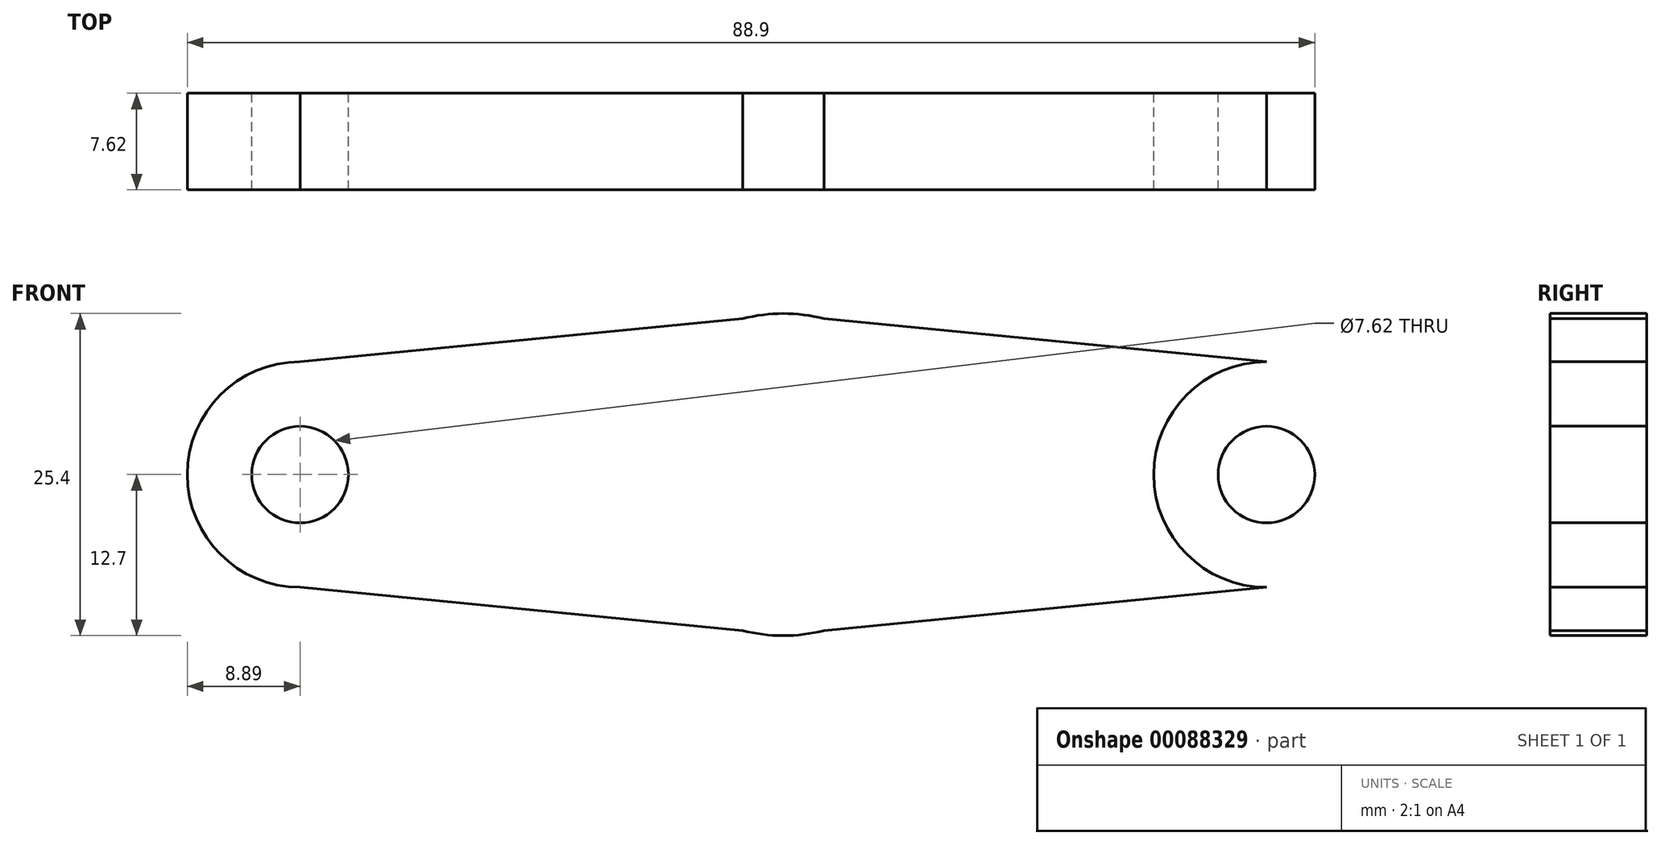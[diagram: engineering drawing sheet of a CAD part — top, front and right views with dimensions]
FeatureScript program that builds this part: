
annotation { "Feature Type Name" : "Feature", "Feature Type Description" : "" }
export const myFeature = defineFeature(function(context is Context, id is Id, definition is map)
    precondition{}
    {
        {
            var Q0;
            Q0=qCreatedBy(makeId("Front.planeOp"),FACE);
            var sketch = newSketch(context, id + "F0", { "sketchPlane" : qUnion([Q0])});
            skCircle(sketch, "E0", {"center": v(0, 0) * mm, "radius": 12.7 * mm});
            skLineSegment(sketch, "E1", {"start": v(0, 0) * mm, "end": v(-38.1, 0) * mm});
            skCircle(sketch, "E2", {"center": v(-38.1, 0) * mm, "radius": 3.81 * mm});
            skCircle(sketch, "E3", {"center": v(-38.1, 0) * mm, "radius": 8.9 * mm});
            skLineSegment(sketch, "E4", {"start": v(-38.1, 0) * mm, "end": v(-38.1, 8.89) * mm});
            skLineSegment(sketch, "E5", {"start": v(-38.1, 8.89) * mm, "end": v(-3.2, 12.3) * mm});
            skLineSegment(sketch, "E6.MirrorCS", {"start": v(-38.1, -8.9) * mm, "end": v(-3.2, -12.3) * mm});
            skCircle(sketch, "E7.MirrorC", {"center": v(38.1, 0) * mm, "radius": 8.9 * mm});
            skLineSegment(sketch, "E8.MirrorCS", {"start": v(38.1, 8.9) * mm, "end": v(3.2, 12.3) * mm});
            skLineSegment(sketch, "E9.MirrorCS", {"start": v(38.1, -8.89) * mm, "end": v(3.2, -12.3) * mm});
            skCircle(sketch, "E10.MirrorC", {"center": v(38.1, 0) * mm, "radius": 3.81 * mm});
            skLineSegment(sketch, "E11.MirrorCS", {"start": v(38.1, 0) * mm, "end": v(38.1, 8.9) * mm});
            skSolve(sketch);
        }
        {
            var Q0;
            {var subQ0=sQuery(id+"F0.wireOp",EDGE,"E5");Q0=makeQuery(id+"F0.imprint","IMPRINT",FACE,{"disambiguationData":[TD([[makeQuery(id+"F0.imprint","IMPRINT",EDGE,{"derivedFrom":subQ0}),-1.0]])]});}
            var Q1;
            {var subQ0=sQuery(id+"F0.wireOp",EDGE,"E6.MirrorCS");Q1=makeQuery(id+"F0.imprint","IMPRINT",FACE,{"disambiguationData":[TD([[makeQuery(id+"F0.imprint","IMPRINT",EDGE,{"derivedFrom":subQ0}),1.0]])]});}
            var Q2;
            {var subQ0=sQuery(id+"F0.wireOp",EDGE,"E8.MirrorCS");Q2=makeQuery(id+"F0.imprint","IMPRINT",FACE,{"disambiguationData":[TD([[makeQuery(id+"F0.imprint","IMPRINT",EDGE,{"derivedFrom":subQ0}),1.0]])]});}
            var Q3;
            {var subQ0=sQuery(id+"F0.wireOp",EDGE,"E3");var subQ2=sQuery(id+"F0.wireOp",EDGE,"E1");var subQ3=makeQuery(id+"F0.imprint","INTERSECT",VERTEX,{"derivedFrom":[subQ2,subQ0]});Q3=makeQuery(id+"F0.imprint","IMPRINT",FACE,{"disambiguationData":[TD([[makeQuery(id+"F0.imprint","IMPRINT",EDGE,{"disambiguationData":[TD([[subQ3,-1.0]])],"derivedFrom":subQ2}),1.0]])]});}
            var Q4;
            {var subQ0=sQuery(id+"F0.wireOp",EDGE,"E3");var subQ1=sQuery(id+"F0.wireOp",EDGE,"E1");var subQ2=makeQuery(id+"F0.imprint","INTERSECT",VERTEX,{"derivedFrom":[subQ1,subQ0]});Q4=makeQuery(id+"F0.imprint","IMPRINT",FACE,{"disambiguationData":[TD([[makeQuery(id+"F0.imprint","IMPRINT",EDGE,{"disambiguationData":[TD([[subQ2,-1.0]])],"derivedFrom":subQ1}),-1.0]])]});}
            var Q5;
            {var subQ0=sQuery(id+"F0.wireOp",EDGE,"E0");var subQ4=makeQuery(id+"F0.imprint","INTERSECT",VERTEX,{"derivedFrom":[subQ0,sQuery(id+"F0.wireOp",EDGE,"E5")]});Q5=makeQuery(id+"F0.imprint","IMPRINT",FACE,{"disambiguationData":[TD([[makeQuery(id+"F0.imprint","IMPRINT",EDGE,{"disambiguationData":[TD([[subQ4,1.0]])],"derivedFrom":subQ0}),1.0]])]});}
            var Q6;
            Q6=makeQuery(id+"F0.imprint","IMPRINT",FACE,{"disambiguationData":[TD([[makeQuery(id+"F0.imprint","IMPRINT",EDGE,{"derivedFrom":sQuery(id+"F0.wireOp",EDGE,"E10.MirrorC")}),1.0]])]});
            extrude(context, id + "F1", {"entities" : qUnion([Q0, Q1, Q2, Q3, Q4, Q5, Q6]), "depth" : 7.62 * mm});
        }
    });
